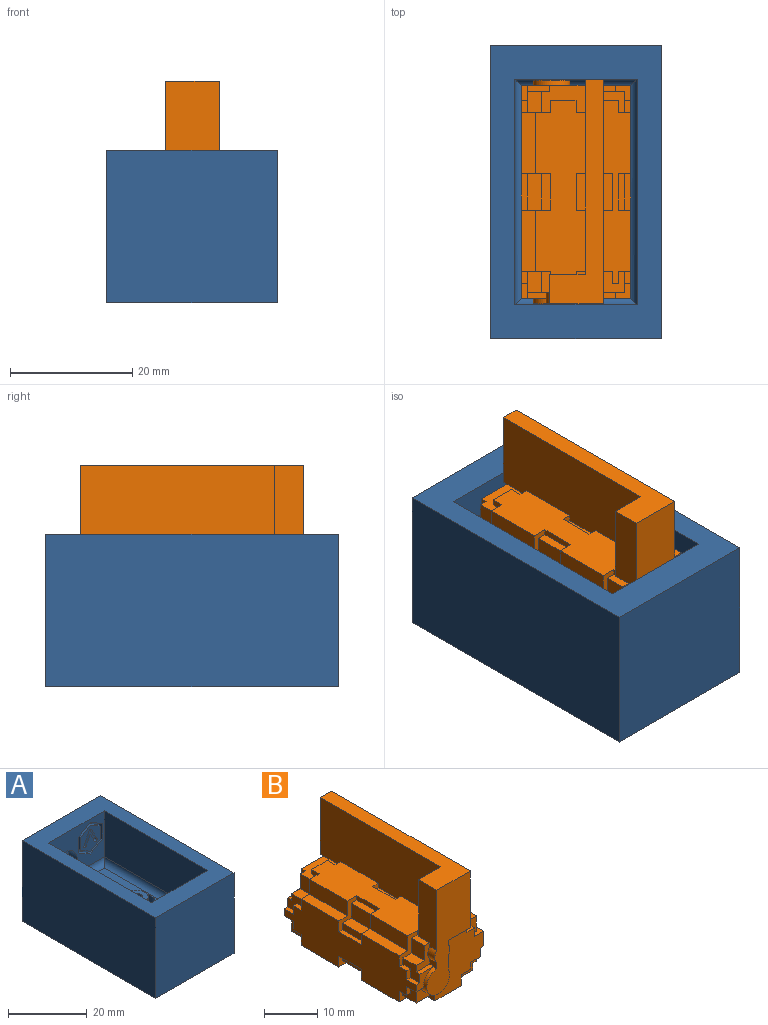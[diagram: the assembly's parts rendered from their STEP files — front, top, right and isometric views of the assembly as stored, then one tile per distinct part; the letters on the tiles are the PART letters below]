
ASSEMBLY  parts=2 mates=1
PART A: 53 faces, bbox 28x48x25 mm
  f0: plane 20x14.25mm, normal (0,-1,0), area 165.7mm2, adj f5,f7,f9,f16,f32,f33,f34,f35
  f1: plane 48x25mm, normal (-1,0,0), area 1200mm2, adj f2,f4,f5,f6
  f2: plane 28x25mm, normal (0,-1,0), area 700mm2, adj f1,f3,f5,f6
  f3: plane 48x25mm, normal (1,0,0), area 1200mm2, adj f2,f4,f5,f6
  f4: plane 28x25mm, normal (0,1,0), area 661mm2, adj f1,f3,f5,f6,f18,f19,f20,f21
  f5: plane 48x28mm, normal (0,0,1), area 604mm2, adj f0,f1,f2,f3,f4,f7,f8,f9
  f6: plane 48x28mm, normal (0,0,-1), area 1336.2mm2, adj f1,f2,f3,f4,f13
  f7: plane 37x14.25mm, normal (1,0,0), area 527.2mm2, adj f0,f5,f8,f49
  f8: plane 20x14.25mm, normal (0,1,0), area 285mm2, adj f5,f7,f9,f51
  f9: plane 37x14.25mm, normal (-1,0,0), area 527.2mm2, adj f0,f5,f8,f52
  f10: plane 33.5x16.5mm, normal (0,0,1), area 474.2mm2, adj f11,f49,f50,f51,f52
  f11: cylinder r=5mm len=10mm, axis (0,0,1), area 125.7mm2, adj f10,f12
  f12: plane 10x10mm, normal (0,0,1), area 50.3mm2, adj f11,f15
  f13: cylinder r=1.57mm len=11mm, axis (0,0,-1), area 108.9mm2, adj f6,f14
  f14: plane 6x6mm, normal (0,0,1), area 20.5mm2, adj f13,f15
  f15: cylinder r=3mm len=6mm, axis (0,0,-1), area 113.1mm2, adj f12,f14
  f16: cylinder r=4.25mm len=8.5mm, axis (0,-1,0), area 80.1mm2, adj f0,f17
  f17: plane 8.5x8.5mm, normal (0,-1,0), area 56.7mm2, adj f16
  f18: cylinder r=1mm len=2mm, axis (0,1,0), area 3.1mm2, adj f4,f19,f25,f26
  f19: plane 4.5x1mm, normal (0,0,-1), area 4.5mm2, adj f4,f18,f20,f26
  f20: cylinder r=0.5mm len=1mm, axis (0,1,0), area 0.8mm2, adj f4,f19,f21,f26
  f21: plane 10.5x1mm, normal (1,0,0), area 10.5mm2, adj f4,f20,f22,f26
  f22: cylinder r=1mm len=2mm, axis (0,1,0), area 3.1mm2, adj f4,f21,f23,f26
  f23: plane 12x1mm, normal (-1,0,0), area 12mm2, adj f4,f22,f24,f26
  f24: cylinder r=1mm len=1mm, axis (0,1,0), area 1.6mm2, adj f4,f23,f25,f26
  f25: plane 6x1mm, normal (0,0,1), area 6mm2, adj f4,f18,f24,f26
  f26: plane 14x8mm, normal (0,1,0), area 39mm2, adj f18,f19,f20,f21,f22,f23,f24,f25
  f27: plane 3.5x2.02mm, normal (0.5,0,-0.87), area 4mm2, adj f28,f38,f39,f40
  f28: plane 3.5x2.02mm, normal (-0.5,0,-0.87), area 4mm2, adj f27,f29,f39,f40
  f29: plane 4.04x1mm, normal (-1,0,0), area 4mm2, adj f28,f30,f39,f40
  f30: plane 3.5x2.02mm, normal (-0.5,0,0.87), area 4mm2, adj f29,f31,f39,f40
  f31: plane 3.5x2.02mm, normal (0.5,0,0.87), area 4mm2, adj f30,f38,f39,f40
  f32: plane 4.91x1mm, normal (-1,0,0), area 4.9mm2, adj f0,f33,f37,f39
  f33: plane 4.25x2.45mm, normal (-0.5,0,-0.87), area 4.9mm2, adj f0,f32,f34,f39
  f34: plane 4.25x2.45mm, normal (0.5,0,-0.87), area 4.9mm2, adj f0,f33,f35,f39
  f35: plane 4.91x1mm, normal (1,0,0), area 4.9mm2, adj f0,f34,f36,f39
  f36: plane 4.25x2.45mm, normal (0.5,0,0.87), area 4.9mm2, adj f0,f35,f37,f39
  f37: plane 4.25x2.45mm, normal (-0.5,0,0.87), area 4.9mm2, adj f0,f32,f36,f39
  f38: plane 4.04x1mm, normal (1,0,0), area 4mm2, adj f27,f31,f39,f40
  f39: plane 9.82x8.5mm, normal (0,-1,0), area 20.1mm2, adj f27,f28,f29,f30,f31,f32,f33,f34
  f40: plane 8.08x7mm, normal (0,-1,0), area 33.5mm2, adj f27,f28,f29,f30,f31,f38,f41,f42
  f41: cylinder r=0.5mm len=1mm, axis (0,-1,0), area 1.6mm2, adj f40,f42,f47,f48
  f42: plane 2.88x1.5mm, normal (-0.89,0,0.46), area 3.2mm2, adj f40,f41,f43,f48
  f43: plane 2.88x1.5mm, normal (0.89,0,0.46), area 3.2mm2, adj f40,f42,f44,f48
  f44: cylinder r=0.5mm len=1mm, axis (0,-1,0), area 1.6mm2, adj f40,f43,f45,f48
  f45: plane 3.73x1.94mm, normal (-0.89,0,-0.46), area 4.2mm2, adj f40,f44,f46,f48
  f46: cylinder r=0.5mm len=1mm, axis (0,-1,0), area 1.1mm2, adj f40,f45,f47,f48
  f47: plane 3.73x1.94mm, normal (0.89,0,-0.46), area 4.2mm2, adj f40,f41,f46,f48
  f48: plane 4.88x4.73mm, normal (0,-1,0), area 9mm2, adj f41,f42,f43,f44,f45,f46,f47
  f49: cylinder r=1.75mm len=37mm, axis (0,-1,0), area 98.2mm2, adj f7,f10,f50,f51
  f50: cylinder r=1.75mm len=20mm, axis (-1,0,0), area 51.5mm2, adj f0,f10,f49,f52
  f51: cylinder r=1.75mm len=20mm, axis (1,0,0), area 51.5mm2, adj f8,f10,f49,f52
  f52: cylinder r=1.75mm len=37mm, axis (0,1,0), area 98.2mm2, adj f9,f10,f50,f51
PART B: 170 faces, bbox 18x36.7x36 mm
  f0: plane 4x3.5mm, normal (0,-1,0), area 8.4mm2, adj f2,f14,f39,f91,f143
  f1: plane 1.85x1.39mm, normal (-1,0,0), area 2.5mm2, adj f2,f33,f53,f56,f168,f169
  f2: cylinder r=3mm len=6mm, axis (0,1,0), area 17.2mm2, adj f0,f1,f56,f91,f110,f143,f167,f169
  f3: cylinder r=2mm len=2.53mm, axis (0,1,0), area 2.3mm2, adj f56,f110,f111,f167
  f4: plane 3.5x3.5mm, normal (0,-1,0), area 8.2mm2, adj f29,f42,f61,f79,f165,f166
  f5: plane 5x3.1mm, normal (0,-1,0), area 9.9mm2, adj f15,f18,f19,f41,f142,f162,f163,f164
  f6: plane 3x0.85mm, normal (0,0,-1), area 2.5mm2, adj f28,f59,f61,f161
  f7: plane 4x3.5mm, normal (0,1,0), area 8.4mm2, adj f10,f12,f35,f103,f149
  f8: plane 6.54x3.1mm, normal (0,1,0), area 12.2mm2, adj f11,f45,f49,f50,f150,f158,f159,f160
  f9: plane 3.5x3.5mm, normal (0,1,0), area 8.2mm2, adj f31,f44,f61,f69,f156,f157
  f10: cylinder r=3mm len=6mm, axis (0,1,0), area 20.2mm2, adj f7,f55,f103,f149,f161
  f11: plane 5.54x3.5mm, normal (0,0,-1), area 14.4mm2, adj f8,f49,f65,f150,f151,f152
  f12: plane 4x3.5mm, normal (0,0,-1), area 9mm2, adj f7,f35,f106,f147,f148,f149
  f13: plane 6x1.5mm, normal (0,0,-1), area 9mm2, adj f40,f85,f87,f146
  f14: plane 4x3.5mm, normal (0,0,-1), area 9mm2, adj f0,f39,f88,f143,f144,f145
  f15: plane 4x3.5mm, normal (0,0,-1), area 9mm2, adj f5,f18,f83,f140,f141,f142
  f16: plane 6x1.6mm, normal (1,0,0), area 9.6mm2, adj f17,f48,f62,f64
  f17: plane 6x1mm, normal (0,0,-1), area 6mm2, adj f16,f46,f62,f64
  f18: plane 3.5x1.6mm, normal (1,0,0), area 5.6mm2, adj f5,f15,f19,f83
  f19: plane 3.5x1mm, normal (0,0,-1), area 3.5mm2, adj f5,f18,f41,f83
  f20: plane 6x3.4mm, normal (-1,0,0), area 20.4mm2, adj f23,f25,f96,f98
  f21: plane 3.5x3.4mm, normal (-1,0,0), area 11.9mm2, adj f24,f52,f53,f95
  f22: plane 3.5x2.3mm, normal (0,0,1), area 8.1mm2, adj f36,f51,f54,f99
  f23: plane 6x2.3mm, normal (0,0,1), area 13.8mm2, adj f20,f37,f96,f98
  f24: plane 3.5x1.5mm, normal (0,0,1), area 4.8mm2, adj f21,f53,f95,f108,f109,f133
  f25: plane 6x1.5mm, normal (0,0,1), area 9mm2, adj f20,f96,f98,f132
  f26: plane 7.2x4.5mm, normal (0,0,1), area 22.7mm2, adj f28,f51,f54,f99,f128,f129,f130,f131
  f27: plane 1.5x0.5mm, normal (0,0,1), area 0.7mm2, adj f28,f108,f123,f124
  f28: plane 31.85x13mm, normal (-1,0,0), area 394.1mm2, adj f6,f26,f27,f34,f59,f60,f108,f124
  f29: plane 3.5x3.5mm, normal (0,0,1), area 10.3mm2, adj f4,f42,f61,f76,f112,f113,f114,f115
  f30: plane 6x1.5mm, normal (0,0,1), area 9mm2, adj f61,f119,f120,f121
  f31: plane 3.5x3.5mm, normal (0,0,1), area 7.3mm2, adj f9,f44,f61,f72,f117,f118
  f32: plane 5.85x0.85mm, normal (0,0,-1), area 5mm2, adj f56,f61,f111,f167
  f33: cylinder r=2mm len=2.76mm, axis (0,1,0), area 5.6mm2, adj f1,f53,f56,f109
  f34: plane 6x1.5mm, normal (0,0,1), area 9mm2, adj f28,f125,f126,f127
  f35: plane 3.5x3.5mm, normal (-1,0,0), area 8.3mm2, adj f7,f12,f103,f104,f105,f106
  f36: plane 4.5x3.5mm, normal (-1,0,0), area 10.3mm2, adj f22,f54,f99,f100,f101,f102,f154,f161
  f37: plane 6x1.5mm, normal (-1,0,0), area 9mm2, adj f23,f96,f97,f98
  f38: plane 4.5x3.5mm, normal (-1,0,0), area 10.3mm2, adj f52,f53,f92,f93,f94,f95,f168,f169
  f39: plane 3.5x3.5mm, normal (-1,0,0), area 8.3mm2, adj f0,f14,f88,f89,f90,f91
  f40: plane 6x1.5mm, normal (-1,0,0), area 9mm2, adj f13,f85,f86,f87
  f41: plane 4.5x3.5mm, normal (1,0,0), area 10.3mm2, adj f5,f19,f80,f81,f82,f83,f164,f167
  f42: plane 3.5x3.5mm, normal (1,0,0), area 8.3mm2, adj f4,f29,f76,f77,f78,f79
  f43: plane 6x1.5mm, normal (1,0,0), area 9mm2, adj f47,f73,f74,f75
  f44: plane 3.5x3.5mm, normal (1,0,0), area 8.3mm2, adj f9,f31,f69,f70,f71,f72
  f45: plane 4.5x3.5mm, normal (1,0,0), area 10.3mm2, adj f8,f50,f65,f66,f67,f68,f158,f161
  f46: plane 6x1.5mm, normal (1,0,0), area 9mm2, adj f17,f62,f63,f64
  f47: plane 6x1mm, normal (0,0,1), area 6mm2, adj f43,f73,f75,f116
  f48: plane 7.15x6.3mm, normal (0,0,-1), area 32.7mm2, adj f16,f57,f62,f64,f139
  f49: plane 3.5x1.6mm, normal (1,0,0), area 5.6mm2, adj f8,f11,f50,f65
  f50: plane 3.5x1mm, normal (0,0,-1), area 3.5mm2, adj f8,f45,f49,f65
  f51: plane 3.5x3.4mm, normal (-1,0,0), area 11.9mm2, adj f22,f26,f54,f99
  f52: plane 3.5x2.3mm, normal (0,0,1), area 8.1mm2, adj f21,f38,f53,f95
  f53: plane 4.9x3.65mm, normal (0,-1,0), area 9mm2, adj f1,f21,f24,f33,f38,f52,f109,f168
  f54: plane 4.9x3.65mm, normal (0,1,0), area 10.1mm2, adj f22,f26,f36,f51,f154,f155
  f55: plane 6x6mm, normal (0,1,0), area 28.3mm2, adj f10
  f56: plane 24x11.5mm, normal (0,-1,0), area 161.4mm2, adj f1,f2,f3,f32,f33,f60,f61,f109
  f57: cylinder r=1.5mm len=11mm, axis (0,0,1), area 103.7mm2, adj f48,f58
  f58: plane 3x3mm, normal (0,0,-1), area 7.1mm2, adj f57
  f59: plane 13x3mm, normal (0,1,0), area 39mm2, adj f6,f28,f60,f61
  f60: plane 36.7x8.85mm, normal (0,0,1), area 138.5mm2, adj f28,f56,f59,f61,f108,f109
  f61: plane 36.7x14.5mm, normal (1,0,0), area 458.1mm2, adj f4,f6,f9,f29,f30,f31,f32,f56
  f62: plane 5.04x4.1mm, normal (0,1,0), area 9.7mm2, adj f16,f17,f46,f48,f63,f84,f139,f153
  f63: plane 6x1mm, normal (0,0,-1), area 6mm2, adj f46,f62,f64,f84
  f64: plane 5.04x4.1mm, normal (0,-1,0), area 9.7mm2, adj f16,f17,f46,f48,f63,f84,f139,f153
  f65: plane 5.04x4.1mm, normal (0,1,0), area 9.7mm2, adj f11,f45,f49,f50,f66,f84,f152,f153
  f66: plane 2x1mm, normal (0,0,-1), area 2mm2, adj f45,f65,f67,f84
  f67: plane 2x1mm, normal (0,1,0), area 2mm2, adj f45,f66,f68,f84
  f68: plane 2.5x1mm, normal (0,0,-1), area 2.5mm2, adj f45,f67,f84,f161
  f69: plane 2.5x2.5mm, normal (0,0,1), area 4mm2, adj f9,f44,f70,f84,f157,f161
  f70: plane 2x1mm, normal (0,1,0), area 2mm2, adj f44,f69,f71,f84
  f71: plane 2x1mm, normal (0,0,1), area 2mm2, adj f44,f70,f72,f84
  f72: plane 2.5x2mm, normal (0,1,0), area 3.5mm2, adj f31,f44,f71,f84,f117,f122
  f73: plane 2.5x2mm, normal (0,-1,0), area 3.5mm2, adj f43,f47,f74,f84,f116,f122
  f74: plane 6x1mm, normal (0,0,1), area 6mm2, adj f43,f73,f75,f84
  f75: plane 2.5x2mm, normal (0,1,0), area 3.5mm2, adj f43,f47,f74,f84,f116,f122
  f76: plane 2.5x2mm, normal (0,-1,0), area 3.5mm2, adj f29,f42,f77,f84,f115,f122
  f77: plane 2x1mm, normal (0,0,1), area 2mm2, adj f42,f76,f78,f84
  f78: plane 2x1mm, normal (0,-1,0), area 2mm2, adj f42,f77,f79,f84
  f79: plane 2.5x2.5mm, normal (0,0,1), area 4mm2, adj f4,f42,f78,f84,f165,f167
  f80: plane 2.5x1mm, normal (0,0,-1), area 2.5mm2, adj f41,f81,f84,f167
  f81: plane 2x1mm, normal (0,-1,0), area 2mm2, adj f41,f80,f82,f84
  f82: plane 2x1mm, normal (0,0,-1), area 2mm2, adj f41,f81,f83,f84
  f83: plane 4.1x3.5mm, normal (0,-1,0), area 8.2mm2, adj f15,f18,f19,f41,f82,f84,f140,f153
  f84: plane 35x14mm, normal (1,0,0), area 371mm2, adj f62,f63,f64,f65,f66,f67,f68,f69
  f85: plane 2.5x2.5mm, normal (0,-1,0), area 4mm2, adj f13,f40,f86,f107,f146,f153
  f86: plane 6x1mm, normal (0,0,-1), area 6mm2, adj f40,f85,f87,f107
  f87: plane 2.5x2.5mm, normal (0,1,0), area 4mm2, adj f13,f40,f86,f107,f146,f153
  f88: plane 2.5x2.5mm, normal (0,-1,0), area 4mm2, adj f14,f39,f89,f107,f145,f153
  f89: plane 2x1mm, normal (0,0,-1), area 2mm2, adj f39,f88,f90,f107
  f90: plane 2x1mm, normal (0,-1,0), area 2mm2, adj f39,f89,f91,f107
  f91: plane 2.5x2.04mm, normal (0,0,-1), area 3.5mm2, adj f0,f2,f39,f90,f107,f169
  f92: plane 2.5x1mm, normal (0,0,1), area 2.5mm2, adj f38,f93,f107,f169
  f93: plane 2x1mm, normal (0,-1,0), area 2mm2, adj f38,f92,f94,f107
  f94: plane 2x1mm, normal (0,0,1), area 2mm2, adj f38,f93,f95,f107
  f95: plane 5.9x4.8mm, normal (0,-1,0), area 9.7mm2, adj f21,f24,f38,f52,f94,f107,f133,f134
  f96: plane 5.9x4.8mm, normal (0,1,0), area 9.7mm2, adj f20,f23,f25,f37,f97,f107,f132,f134
  f97: plane 6x1mm, normal (0,0,1), area 6mm2, adj f37,f96,f98,f107
  f98: plane 5.9x4.8mm, normal (0,-1,0), area 9.7mm2, adj f20,f23,f25,f37,f97,f107,f132,f134
  f99: plane 5.9x4.8mm, normal (0,1,0), area 9.7mm2, adj f22,f26,f36,f51,f100,f107,f131,f134
  f100: plane 2x1mm, normal (0,0,1), area 2mm2, adj f36,f99,f101,f107
  f101: plane 2x1mm, normal (0,1,0), area 2mm2, adj f36,f100,f102,f107
  f102: plane 2.5x1mm, normal (0,0,1), area 2.5mm2, adj f36,f101,f107,f161
  f103: plane 2.5x2.04mm, normal (0,0,-1), area 3.5mm2, adj f7,f10,f35,f104,f107,f161
  f104: plane 2x1mm, normal (0,1,0), area 2mm2, adj f35,f103,f105,f107
  f105: plane 2x1mm, normal (0,0,-1), area 2mm2, adj f35,f104,f106,f107
  f106: plane 2.5x2.5mm, normal (0,1,0), area 4mm2, adj f12,f35,f105,f107,f147,f153
  f107: plane 35x10.6mm, normal (-1,0,0), area 276mm2, adj f85,f86,f87,f88,f89,f90,f91,f92
  f108: plane 13x5.85mm, normal (0,1,0), area 71.8mm2, adj f24,f27,f28,f60,f109,f123,f133,f134
  f109: plane 13.87x4.85mm, normal (-1,0,0), area 64.7mm2, adj f24,f33,f53,f56,f60,f108
  f110: plane 3.08x0.85mm, normal (1,0,0), area 2.6mm2, adj f2,f3,f56,f167
  f111: plane 0.99x0.85mm, normal (1,0,0), area 0.8mm2, adj f3,f32,f56,f167
  f112: plane 1.5x1mm, normal (0,-1,0), area 1.5mm2, adj f29,f61,f113,f122
  f113: plane 2x1mm, normal (-1,0,0), area 2mm2, adj f29,f112,f114,f122
  f114: plane 1x1mm, normal (0,-1,0), area 1mm2, adj f29,f113,f115,f122
  f115: plane 2x1mm, normal (1,0,0), area 2mm2, adj f29,f76,f114,f122
  f116: plane 6x1mm, normal (1,0,0), area 6mm2, adj f47,f73,f75,f122
  f117: plane 2x1mm, normal (1,0,0), area 2mm2, adj f31,f72,f118,f122
  f118: plane 2.5x1mm, normal (0,1,0), area 2.5mm2, adj f31,f61,f117,f122
  f119: plane 1.5x1mm, normal (0,-1,0), area 1.5mm2, adj f30,f61,f120,f122
  f120: plane 6x1mm, normal (-1,0,0), area 6mm2, adj f30,f119,f121,f122
  f121: plane 1.5x1mm, normal (0,1,0), area 1.5mm2, adj f30,f61,f120,f122
  f122: plane 30x4.5mm, normal (0,0,1), area 103mm2, adj f61,f72,f73,f75,f76,f84,f112,f113
  f123: plane 1x0.5mm, normal (1,0,0), area 0.5mm2, adj f27,f108,f124,f134
  f124: plane 1.5x1mm, normal (0,-1,0), area 1.5mm2, adj f27,f28,f123,f134
  f125: plane 1.5x1mm, normal (0,1,0), area 1.5mm2, adj f28,f34,f126,f134
  f126: plane 6x1mm, normal (1,0,0), area 6mm2, adj f34,f125,f127,f134
  f127: plane 1.5x1mm, normal (0,-1,0), area 1.5mm2, adj f28,f34,f126,f134
  f128: plane 1.5x1mm, normal (0,1,0), area 1.5mm2, adj f26,f28,f129,f134
  f129: plane 2x1mm, normal (1,0,0), area 2mm2, adj f26,f128,f130,f134
  f130: plane 4.2x1mm, normal (0,1,0), area 4.2mm2, adj f26,f129,f131,f134
  f131: plane 2x1mm, normal (-1,0,0), area 2mm2, adj f26,f99,f130,f134
  f132: plane 6x1mm, normal (-1,0,0), area 6mm2, adj f25,f96,f98,f134
  f133: plane 1x0.5mm, normal (-1,0,0), area 0.5mm2, adj f24,f95,f108,f134
  f134: plane 28.5x8.2mm, normal (0,0,1), area 199.7mm2, adj f28,f95,f96,f98,f99,f108,f123,f124
  f135: plane 10x2.3mm, normal (0,0,1), area 23mm2, adj f95,f96,f107,f137
  f136: plane 10x2.3mm, normal (0,0,1), area 23mm2, adj f98,f99,f107,f138
  f137: plane 10x3.4mm, normal (-1,0,0), area 34mm2, adj f95,f96,f134,f135
  f138: plane 10x3.4mm, normal (-1,0,0), area 34mm2, adj f98,f99,f134,f136
  f139: cylinder r=3.15mm len=6.3mm, axis (0,0,1), area 11.8mm2, adj f48,f62,f64,f153
  f140: plane 2x1mm, normal (1,0,0), area 2mm2, adj f15,f83,f141,f153
  f141: plane 2.5x1mm, normal (0,-1,0), area 2.5mm2, adj f15,f140,f142,f153
  f142: plane 2.5x2.5mm, normal (1,0,0), area 4mm2, adj f5,f15,f141,f153,f162,f167
  f143: plane 2.5x2mm, normal (-1,0,0), area 3.5mm2, adj f0,f2,f14,f144,f153,f167
  f144: plane 2.5x1mm, normal (0,-1,0), area 2.5mm2, adj f14,f143,f145,f153
  f145: plane 2x1mm, normal (-1,0,0), area 2mm2, adj f14,f88,f144,f153
  f146: plane 6x1mm, normal (-1,0,0), area 6mm2, adj f13,f85,f87,f153
  f147: plane 2x1mm, normal (-1,0,0), area 2mm2, adj f12,f106,f148,f153
  f148: plane 2.5x1mm, normal (0,1,0), area 2.5mm2, adj f12,f147,f149,f153
  f149: plane 2.5x2mm, normal (-1,0,0), area 3.5mm2, adj f7,f10,f12,f148,f153,f161
  f150: plane 2.5x2.5mm, normal (1,0,0), area 4mm2, adj f8,f11,f151,f153,f160,f161
  f151: plane 2.5x1mm, normal (0,1,0), area 2.5mm2, adj f11,f150,f152,f153
  f152: plane 2x1mm, normal (1,0,0), area 2mm2, adj f11,f65,f151,f153
  f153: plane 35x18mm, normal (0,0,-1), area 477.3mm2, adj f62,f64,f65,f83,f84,f85,f87,f88
  f154: plane 3.65x1mm, normal (0,0,1), area 3.7mm2, adj f36,f54,f155,f161
  f155: plane 4.9x1mm, normal (-1,0,0), area 4.9mm2, adj f26,f54,f154,f161
  f156: plane 2x1mm, normal (0,0,1), area 2mm2, adj f9,f61,f157,f161
  f157: plane 2x1mm, normal (1,0,0), area 2mm2, adj f9,f69,f156,f161
  f158: plane 2.5x1mm, normal (0,0,-1), area 2.5mm2, adj f8,f45,f159,f161
  f159: plane 1.6x1mm, normal (1,0,0), area 1.6mm2, adj f8,f158,f160,f161
  f160: plane 4.04x1mm, normal (0,0,-1), area 4mm2, adj f8,f150,f159,f161
  f161: plane 18x13mm, normal (0,1,0), area 125.8mm2, adj f6,f10,f26,f36,f45,f61,f68,f69
  f162: plane 2.5x1mm, normal (0,0,-1), area 2.5mm2, adj f5,f142,f163,f167
  f163: plane 1.6x1mm, normal (1,0,0), area 1.6mm2, adj f5,f162,f164,f167
  f164: plane 2.5x1mm, normal (0,0,-1), area 2.5mm2, adj f5,f41,f163,f167
  f165: plane 2x1mm, normal (1,0,0), area 2mm2, adj f4,f79,f166,f167
  f166: plane 2x1mm, normal (0,0,1), area 2mm2, adj f4,f61,f165,f167
  f167: plane 13x13mm, normal (0,-1,0), area 105.3mm2, adj f2,f3,f32,f41,f61,f79,f80,f84
  f168: plane 3.65x1mm, normal (0,0,1), area 3.7mm2, adj f1,f38,f53,f169
  f169: plane 4.65x3.6mm, normal (0,-1,0), area 7.4mm2, adj f1,f2,f38,f91,f92,f107,f168
PLACE A t=(-13.13,22.86,14.36)mm
PLACE B t=(-35.13,46.86,25.59)mm
MATE cylindrical B.f57 <-> A.f11  axis (0,0,1) through (-24.13,46.86,20.09)mm
